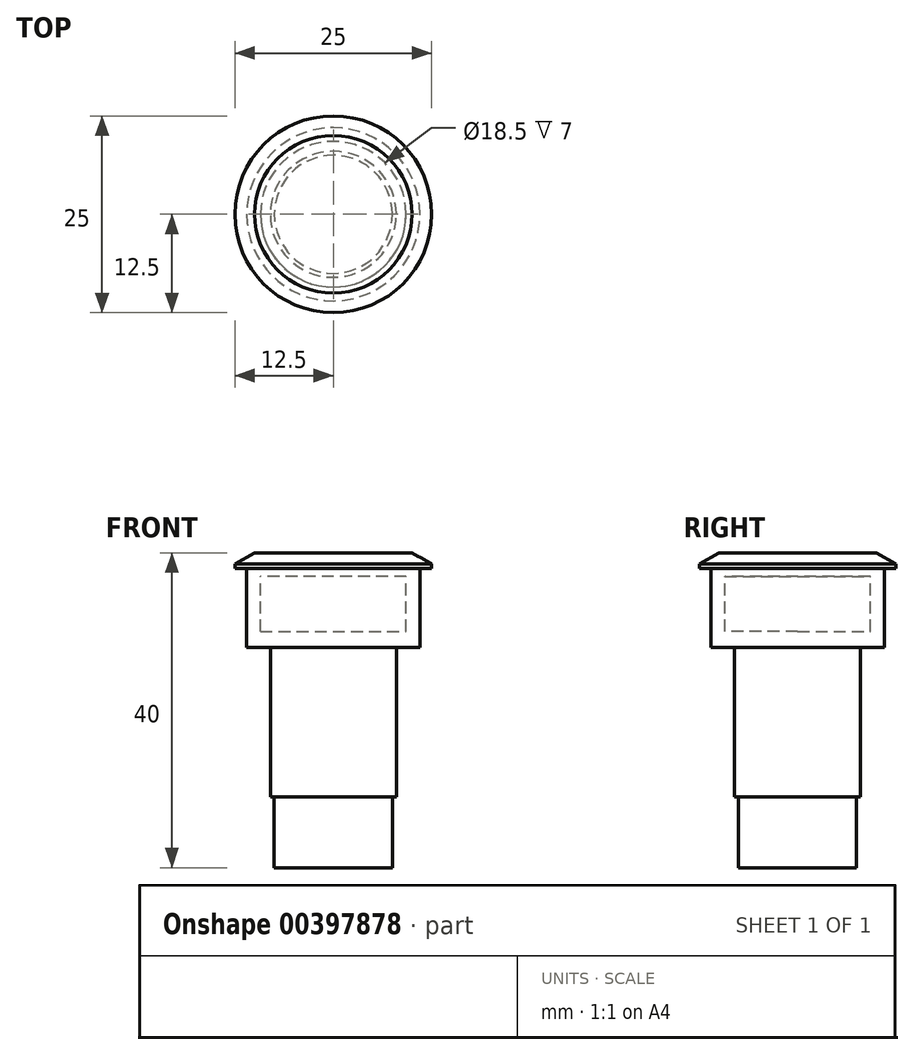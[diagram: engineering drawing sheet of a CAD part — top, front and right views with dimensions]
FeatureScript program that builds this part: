
annotation { "Feature Type Name" : "Feature", "Feature Type Description" : "" }
export const myFeature = defineFeature(function(context is Context, id is Id, definition is map)
    precondition{}
    {
        {
            var Q0;
            Q0=qCreatedBy(makeId("Top.planeOp"),FACE);
            var sketch = newSketch(context, id + "F0", { "sketchPlane" : qUnion([Q0])});
            skCircle(sketch, "E0", {"center": v(0, 0) * mm, "radius": 9.25 * mm});
            skSolve(sketch);
        }
        {
            var Q0;
            Q0 = qSketchRegion(id + "F0", true);
            extrude(context, id + "F1", {"entities" : qUnion([Q0]), "depth" : 3 * mm});
        }
        {
            var Q0;
            Q0=makeQuery(id+"F1.opExtrude","CAP_FACE",FACE,{"disambiguationData":[OSD([sQuery(id+"F0.wireOp",EDGE,"E0")])],"isStart":false});
            var sketch = newSketch(context, id + "F2", { "sketchPlane" : qUnion([Q0])});
            skCircle(sketch, "E1", {"center": v(0, 0) * mm, "radius": 12.5 * mm});
            skCircle(sketch, "E2", {"center": v(0, 0) * mm, "radius": 9.25 * mm});
            skSolve(sketch);
        }
        {
            var Q0;
            Q0 = qSketchRegion(id + "F2", true);
            extrude(context, id + "F3", {"entities" : qUnion([Q0]), "oppositeDirection" : true, "depth" : 2 * mm});
        }
        {
            var Q0;
            Q0=makeQuery(id+"F3.opExtrude","CAP_FACE",FACE,{"disambiguationData":[OSD([sQuery(id+"F2.wireOp",EDGE,"E1"),sQuery(id+"F2.wireOp",EDGE,"E2")])],"isStart":false});
            var sketch = newSketch(context, id + "F4", { "sketchPlane" : qUnion([Q0])});
            skCircle(sketch, "E3", {"center": v(0, 0) * mm, "radius": 11 * mm});
            skCircle(sketch, "E4", {"center": v(0, 0) * mm, "radius": 9.25 * mm});
            skSolve(sketch);
        }
        {
            var Q0;
            Q0 = qSketchRegion(id + "F4", true);
            extrude(context, id + "F5", {"entities" : qUnion([Q0]), "operationType" : NewBodyOperationType.ADD, "depth" : 10 * mm});
        }
        {
            var Q0;
            Q0=makeQuery(id+"F5.opExtrude","CAP_FACE",FACE,{"disambiguationData":[OSD([sQuery(id+"F4.wireOp",EDGE,"E3"),sQuery(id+"F4.wireOp",EDGE,"E4")])],"isStart":false});
            var sketch = newSketch(context, id + "F6", { "sketchPlane" : qUnion([Q0])});
            skCircle(sketch, "E5", {"center": v(0, 0) * mm, "radius": 11 * mm});
            skSolve(sketch);
        }
        {
            var Q0;
            Q0 = qSketchRegion(id + "F6", true);
            extrude(context, id + "F7", {"entities" : qUnion([Q0]), "operationType" : NewBodyOperationType.ADD, "oppositeDirection" : true, "depth" : 2 * mm});
        }
        {
            var Q0;
            Q0=makeQuery(id+"F3.opExtrude","CAP_EDGE",EDGE,{"disambiguationData":[OSD([sQuery(id+"F2.wireOp",EDGE,"E1")])],"isStart":true});
            chamfer(context, id + "F8", {"entities" : qUnion([Q0]), "chamferType" : ChamferType.OFFSET_ANGLE, "width" : 2.5 * mm, "oppositeDirection" : false, "angle" : 30 * degree, "tangentPropagation" : true});
        }
        {
            var Q0;
            Q0=makeQuery(id+"F7.boolean.opBoolean","MERGE",FACE,{"derivedFrom":[makeQuery(id+"F5.opExtrude","CAP_FACE",FACE,{"disambiguationData":[OSD([sQuery(id+"F4.wireOp",EDGE,"E3"),sQuery(id+"F4.wireOp",EDGE,"E4")])],"isStart":false}),makeQuery(id+"F7.opExtrude","CAP_FACE",FACE,{"disambiguationData":[OSD([sQuery(id+"F6.wireOp",EDGE,"E5")])],"isStart":true})]});
            var sketch = newSketch(context, id + "F9", { "sketchPlane" : qUnion([Q0])});
            skCircle(sketch, "E6", {"center": v(0, 0) * mm, "radius": 8 * mm});
            skSolve(sketch);
        }
        {
            var Q0;
            Q0 = qSketchRegion(id + "F9", true);
            extrude(context, id + "F10", {"entities" : qUnion([Q0]), "depth" : 19 * mm});
        }
        {
            var Q0;
            Q0=makeQuery(id+"F10.opExtrude","CAP_FACE",FACE,{"disambiguationData":[OSD([sQuery(id+"F9.wireOp",EDGE,"E6")])],"isStart":false});
            var sketch = newSketch(context, id + "F11", { "sketchPlane" : qUnion([Q0])});
            skCircle(sketch, "E7", {"center": v(0, 0) * mm, "radius": 7.5 * mm});
            skSolve(sketch);
        }
        {
            var Q0;
            Q0 = qSketchRegion(id + "F11", true);
            extrude(context, id + "F12", {"entities" : qUnion([Q0]), "depth" : 9 * mm});
        }
    });
